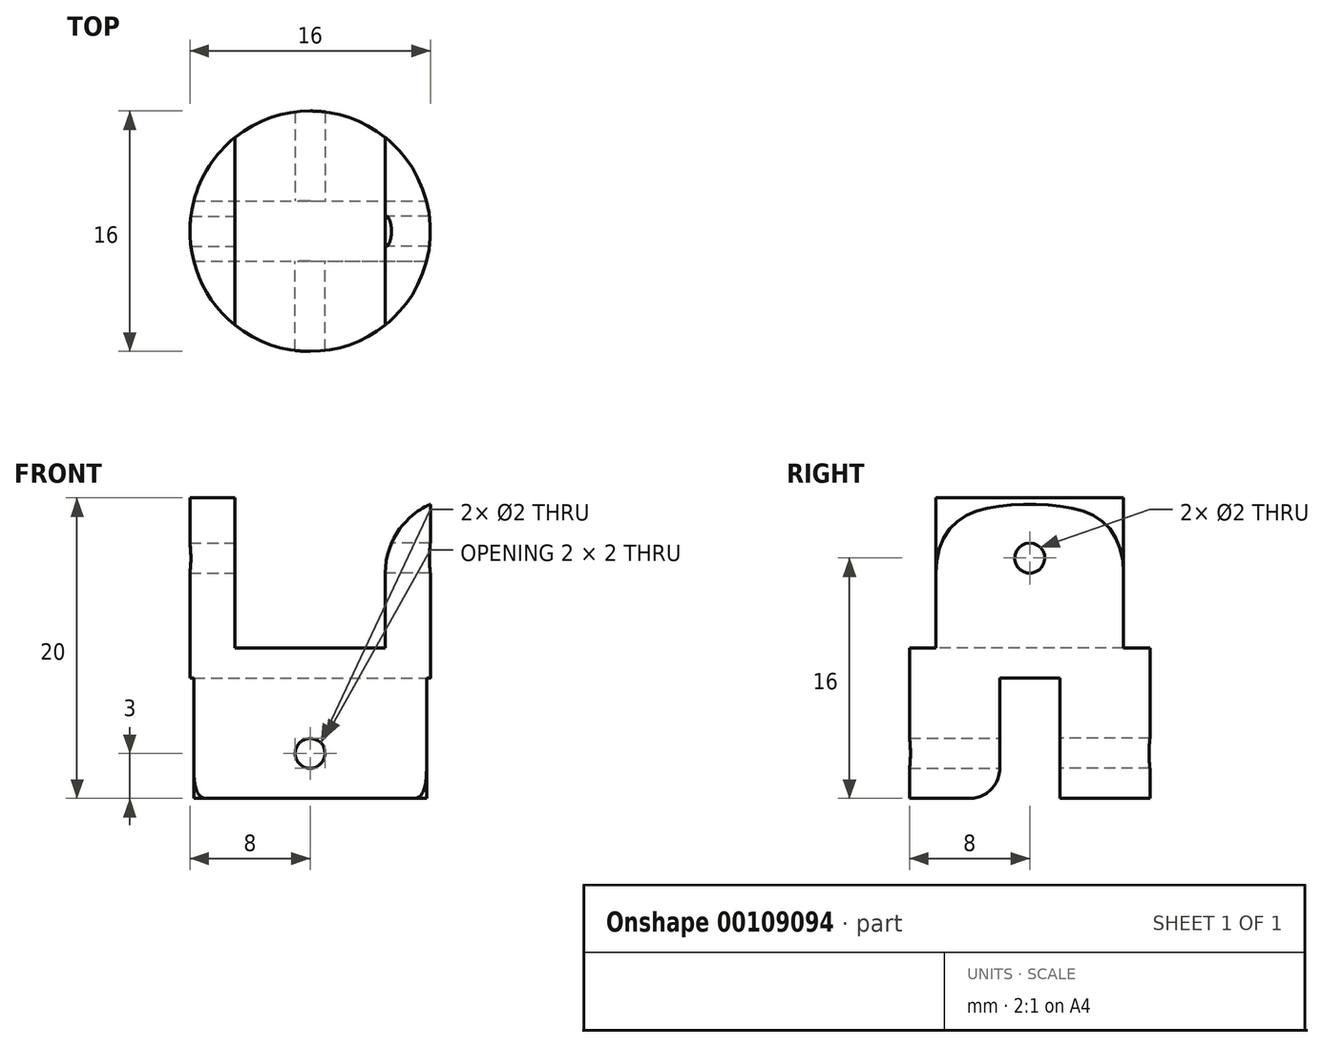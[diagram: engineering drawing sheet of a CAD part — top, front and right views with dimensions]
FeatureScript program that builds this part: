
annotation { "Feature Type Name" : "Feature", "Feature Type Description" : "" }
export const myFeature = defineFeature(function(context is Context, id is Id, definition is map)
    precondition{}
    {
        {
            var Q0;
            Q0=qCreatedBy(makeId("Top.planeOp"),FACE);
            var sketch = newSketch(context, id + "F0", { "sketchPlane" : qUnion([Q0])});
            skCircle(sketch, "E0", {"center": v(0, 0) * mm, "radius": 8 * mm});
            skSolve(sketch);
        }
        {
            var Q0;
            Q0=makeQuery(id+"F0.imprint","IMPRINT",FACE,{"disambiguationData":[TD([[makeQuery(id+"F0.imprint","IMPRINT",EDGE,{"derivedFrom":sQuery(id+"F0.wireOp",EDGE,"E0")}),1.0]])]});
            extrude(context, id + "F1", {"entities" : qUnion([Q0]), "endBound" : BoundingType.SYMMETRIC, "depth" : 20 * mm});
        }
        {
            var Q0;
            Q0=makeQuery(id+"F1.opExtrude","CAP_FACE",FACE,{"disambiguationData":[OSD([sQuery(id+"F0.wireOp",EDGE,"E0")])],"isStart":false});
            var sketch = newSketch(context, id + "F2", { "sketchPlane" : qUnion([Q0])});
            skLineSegment(sketch, "E1", {"start": v(-5, 6.24) * mm, "end": v(-5, -6.24) * mm});
            skLineSegment(sketch, "E2", {"start": v(5, 6.24) * mm, "end": v(5, -6.24) * mm});
            skSolve(sketch);
        }
        {
            var Q0;
            {var subQ0=sQuery(id+"F2.wireOp",EDGE,"E1");Q0=makeQuery(id+"F2.imprint","IMPRINT",FACE,{"disambiguationData":[TD([[makeQuery(id+"F2.imprint","IMPRINT",EDGE,{"derivedFrom":subQ0}),1.0]])]});}
            extrude(context, id + "F3", {"entities" : qUnion([Q0]), "operationType" : NewBodyOperationType.REMOVE, "oppositeDirection" : true, "depth" : 10 * mm});
        }
        {
            var Q0;
            Q0=qCreatedBy(makeId("Right.planeOp"),FACE);
            var sketch = newSketch(context, id + "F4", { "sketchPlane" : qUnion([Q0])});
            skPoint(sketch, "E3", {"position": v(0, 6) * mm});
            skSolve(sketch);
        }
        {
            var Q0;
            Q0=sQuery(id+"F4.wireOp",VERTEX,"E3");
            var Q1;
            Q1=makeQuery(id+"F1.opExtrude","SWEPT_BODY",BODY,{"disambiguationData":[OSD([sQuery(id+"F0.wireOp",EDGE,"E0")])]});
            hole(context, id + "F5", {"style" : HoleStyle.SIMPLE, "endStyle" : HoleEndStyle.THROUGH, "holeDiameter" : 2 * mm, "locations" : qUnion([Q0]), "scope" : qUnion([Q1]), "isTappedThrough" : true});
        }
        {
            var Q0;
            Q0=sQuery(id+"F4.wireOp",VERTEX,"E3");
            var Q1;
            Q1=makeQuery(id+"F1.opExtrude","SWEPT_BODY",BODY,{"disambiguationData":[OSD([sQuery(id+"F0.wireOp",EDGE,"E0")])]});
            hole(context, id + "F6", {"style" : HoleStyle.SIMPLE, "endStyle" : HoleEndStyle.THROUGH, "oppositeDirection" : true, "holeDiameter" : 2 * mm, "locations" : qUnion([Q0]), "scope" : qUnion([Q1]), "isTappedThrough" : true});
        }
        {
            var Q0;
            Q0=makeQuery(id+"F3.boolean.opBoolean","COPY",EDGE,{"derivedFrom":makeQuery(id+"F3.opExtrude","CAP_EDGE",EDGE,{"disambiguationData":[OSD([sQuery(id+"F2.wireOp",EDGE,"E1")])],"isStart":true})});
            var Q1;
            Q1=makeQuery(id+"F3.boolean.opBoolean","COPY",EDGE,{"derivedFrom":makeQuery(id+"F3.opExtrude","CAP_EDGE",EDGE,{"disambiguationData":[OSD([sQuery(id+"F2.wireOp",EDGE,"E2")])],"isStart":true})});
            fillet(context, id + "F7", {"entities" : qUnion([Q0, Q1]), "radius" : 5 * mm, "tangentPropagation" : true, "allowEdgeOverflow" : false});
        }
        {
            var Q0;
            Q0=makeQuery(id+"F1.opExtrude","CAP_FACE",FACE,{"disambiguationData":[OSD([sQuery(id+"F0.wireOp",EDGE,"E0")])],"isStart":true});
            var sketch = newSketch(context, id + "F8", { "sketchPlane" : qUnion([Q0])});
            skLineSegment(sketch, "E4", {"start": v(-7.75, 2) * mm, "end": v(7.75, 2) * mm});
            skLineSegment(sketch, "E5", {"start": v(-7.75, -2) * mm, "end": v(7.75, -2) * mm});
            skSolve(sketch);
        }
        {
            var Q0;
            {var subQ0=sQuery(id+"F8.wireOp",EDGE,"E4");Q0=makeQuery(id+"F8.imprint","IMPRINT",FACE,{"disambiguationData":[TD([[makeQuery(id+"F8.imprint","IMPRINT",EDGE,{"derivedFrom":subQ0}),-1.0]])]});}
            extrude(context, id + "F9", {"entities" : qUnion([Q0]), "operationType" : NewBodyOperationType.REMOVE, "oppositeDirection" : true, "depth" : 8 * mm});
        }
        {
            var Q0;
            Q0=qCreatedBy(makeId("Front.planeOp"),FACE);
            var sketch = newSketch(context, id + "F10", { "sketchPlane" : qUnion([Q0])});
            skPoint(sketch, "E6", {"position": v(0, -7) * mm});
            skSolve(sketch);
        }
        {
            var Q0;
            Q0=sQuery(id+"F10.wireOp",VERTEX,"E6");
            var Q1;
            Q1=makeQuery(id+"F1.opExtrude","SWEPT_BODY",BODY,{"disambiguationData":[OSD([sQuery(id+"F0.wireOp",EDGE,"E0")])]});
            hole(context, id + "F11", {"style" : HoleStyle.SIMPLE, "endStyle" : HoleEndStyle.THROUGH, "holeDiameter" : 2 * mm, "locations" : qUnion([Q0]), "scope" : qUnion([Q1]), "isTappedThrough" : true});
        }
        {
            var Q0;
            Q0=qCreatedBy(makeId("Front.planeOp"),FACE);
            var sketch = newSketch(context, id + "F12", { "sketchPlane" : qUnion([Q0])});
            skPoint(sketch, "E7", {"position": v(0, -7) * mm});
            skSolve(sketch);
        }
        {
            var Q0;
            Q0=sQuery(id+"F12.wireOp",VERTEX,"E7");
            var Q1;
            Q1=makeQuery(id+"F1.opExtrude","SWEPT_BODY",BODY,{"disambiguationData":[OSD([sQuery(id+"F0.wireOp",EDGE,"E0")])]});
            hole(context, id + "F13", {"style" : HoleStyle.SIMPLE, "endStyle" : HoleEndStyle.THROUGH, "oppositeDirection" : true, "holeDiameter" : 2 * mm, "locations" : qUnion([Q0]), "scope" : qUnion([Q1]), "isTappedThrough" : true});
        }
        {
            var Q0;
            Q0=makeQuery(id+"F9.boolean.opBoolean","COPY",EDGE,{"derivedFrom":makeQuery(id+"F9.opExtrude","CAP_EDGE",EDGE,{"disambiguationData":[OSD([sQuery(id+"F8.wireOp",EDGE,"E4")])],"isStart":true})});
            var Q1;
            Q1=makeQuery(id+"F9.boolean.opBoolean","COPY",EDGE,{"derivedFrom":makeQuery(id+"F9.opExtrude","CAP_EDGE",EDGE,{"disambiguationData":[OSD([sQuery(id+"F8.wireOp",EDGE,"E5")])],"isStart":true})});
            fillet(context, id + "F14", {"entities" : qUnion([Q0, Q1]), "radius" : 2 * mm, "tangentPropagation" : true, "allowEdgeOverflow" : false});
        }
    });
